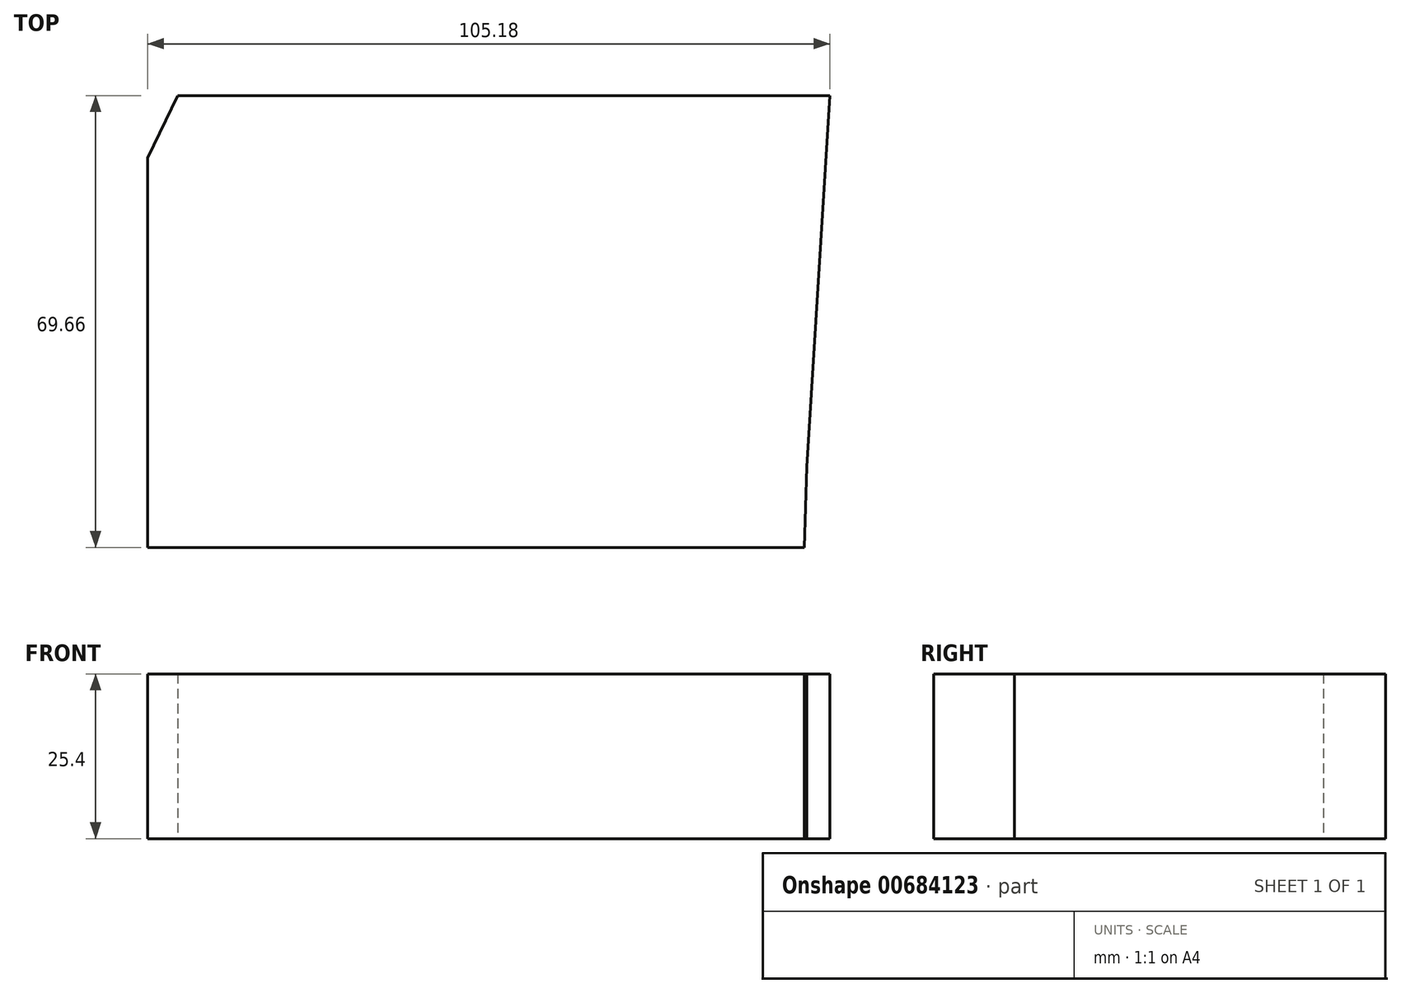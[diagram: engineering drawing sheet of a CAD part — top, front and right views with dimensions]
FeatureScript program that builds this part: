
annotation { "Feature Type Name" : "Feature", "Feature Type Description" : "" }
export const myFeature = defineFeature(function(context is Context, id is Id, definition is map)
    precondition{}
    {
        {
            var Q0;
            Q0=qCreatedBy(makeId("Top.planeOp"),FACE);
            var sketch = newSketch(context, id + "F0", { "sketchPlane" : qUnion([Q0])});
            skLineSegment(sketch, "E0", {"start": v(-43.81, 40.88) * mm, "end": v(56.7, 40.88) * mm});
            skLineSegment(sketch, "E1", {"start": v(56.7, 40.88) * mm, "end": v(56.7, 40.88) * mm});
            skLineSegment(sketch, "E2", {"start": v(53.16, -16.35) * mm, "end": v(56.7, 40.88) * mm});
            skLineSegment(sketch, "E3", {"start": v(52.8, -28.78) * mm, "end": v(53.16, -16.35) * mm});
            skLineSegment(sketch, "E4", {"start": v(52.8, -28.78) * mm, "end": v(-48.48, -28.78) * mm});
            skLineSegment(sketch, "E5", {"start": v(-48.48, -28.78) * mm, "end": v(-48.48, 31.28) * mm});
            skLineSegment(sketch, "E6", {"start": v(-48.48, 31.28) * mm, "end": v(-43.81, 40.88) * mm});
            skLineSegment(sketch, "E7", {"start": v(56.7, 40.88) * mm, "end": v(56.7, 65.38) * mm});
            skSolve(sketch);
        }
        {
            var Q0;
            Q0=makeQuery(id+"F0.imprint","IMPRINT",FACE,{"disambiguationData":[TD([[makeQuery(id+"F0.imprint","IMPRINT",EDGE,{"derivedFrom":sQuery(id+"F0.wireOp",EDGE,"E0")}),-1.0]])]});
            extrude(context, id + "F1", {"entities" : qUnion([Q0]), "depth" : 25.4 * mm, "offsetDistance" : 25.4 * mm});
        }
    });
